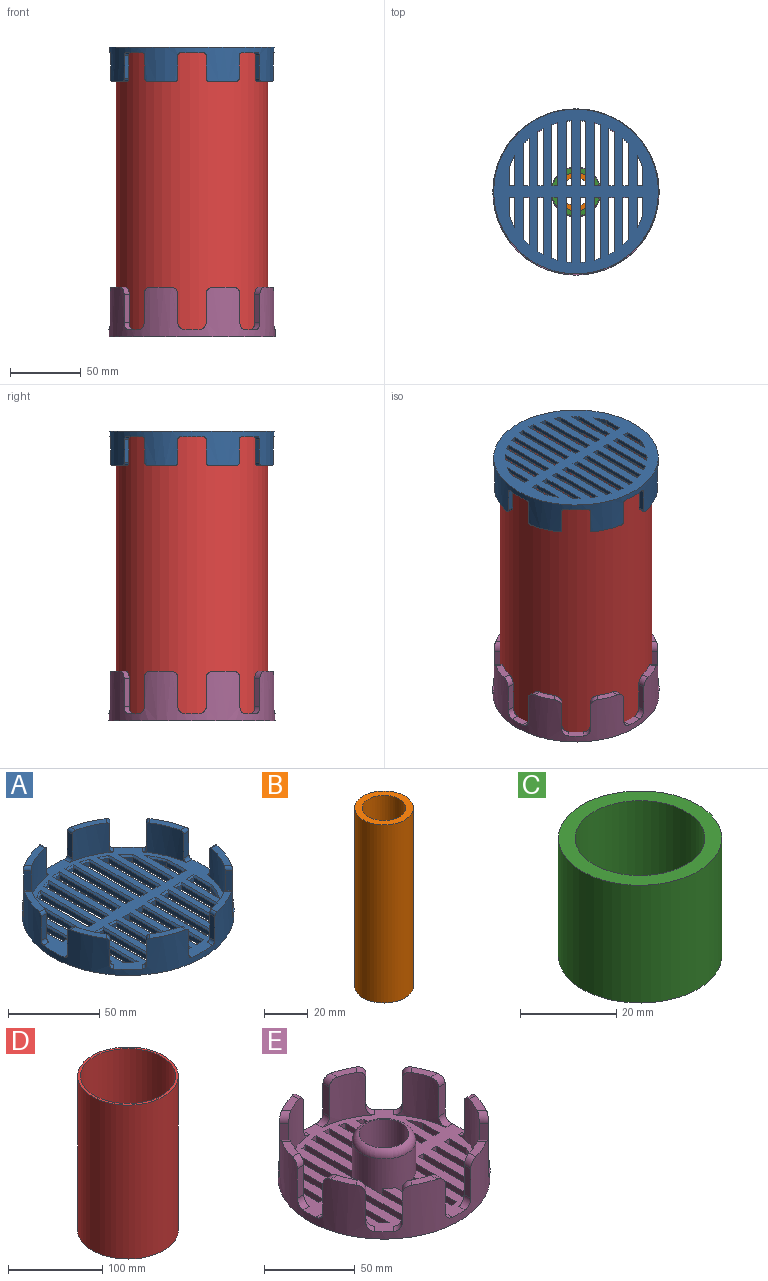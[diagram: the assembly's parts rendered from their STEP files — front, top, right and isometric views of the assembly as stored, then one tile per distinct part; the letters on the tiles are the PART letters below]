
ASSEMBLY  parts=5 mates=4
PART A: 223 faces, bbox 116x116x24 mm
  f0: plane 116x116mm, normal (0,0,-1), area 7720.4mm2, adj f2,f67,f68,f69,f70,f71,f72,f73
  f1: plane 116x116mm, normal (0,0,1), area 5149.1mm2, adj f2,f3,f4,f5,f6,f7,f8,f9
  f2: cylinder r=58mm len=116mm, axis (0,0,1), area 5530.1mm2, adj f0,f1,f10,f11,f12,f13,f14,f15
  f3: cylinder r=54mm len=24.11mm, axis (0,0,-1), area 445.9mm2, adj f1,f10,f19,f33,f42,f43,f51,f54
  f4: cylinder r=54mm len=24.11mm, axis (0,0,-1), area 445.9mm2, adj f1,f11,f32,f34,f41,f44,f53,f56
  f5: cylinder r=54mm len=24.11mm, axis (0,0,-1), area 445.9mm2, adj f1,f12,f30,f31,f40,f45,f55,f57
  f6: cylinder r=54mm len=24.11mm, axis (0,0,-1), area 445.9mm2, adj f1,f13,f26,f27,f37,f46,f62,f65
  f7: cylinder r=54mm len=24.11mm, axis (0,0,-1), area 445.9mm2, adj f1,f14,f24,f25,f36,f47,f60,f63
  f8: cylinder r=54mm len=24.11mm, axis (0,0,-1), area 445.9mm2, adj f1,f15,f22,f23,f35,f48,f58,f61
  f9: cylinder r=54mm len=24.11mm, axis (0,0,-1), area 445.9mm2, adj f1,f16,f20,f21,f49,f50,f52,f59
  f10: plane 19.64x11.03mm, normal (0,0,1), area 79.2mm2, adj f2,f3,f51,f54
  f11: plane 19.64x11.03mm, normal (0,0,1), area 79.2mm2, adj f2,f4,f53,f56
  f12: plane 19.64x11.03mm, normal (0,0,1), area 79.2mm2, adj f2,f5,f55,f57
  f13: plane 19.64x11.03mm, normal (0,0,1), area 79.2mm2, adj f2,f6,f62,f65
  f14: plane 19.64x11.03mm, normal (0,0,1), area 79.2mm2, adj f2,f7,f60,f63
  f15: plane 19.64x11.03mm, normal (0,0,1), area 79.2mm2, adj f2,f8,f58,f61
  f16: plane 19.64x11.03mm, normal (0,0,1), area 79.2mm2, adj f2,f9,f52,f59
  f17: cylinder r=54mm len=24.11mm, axis (0,0,-1), area 445.9mm2, adj f1,f18,f28,f29,f38,f39,f64,f66
  f18: plane 19.64x11.03mm, normal (0,0,1), area 79.2mm2, adj f2,f17,f64,f66
  f19: plane 16x4.07mm, normal (-1,0,0), area 65mm2, adj f2,f3,f42,f51
  f20: plane 16x4.07mm, normal (1,0,0), area 65mm2, adj f2,f9,f50,f52
  f21: plane 16x2.87mm, normal (-0.71,0.71,0), area 65mm2, adj f2,f9,f49,f59
  f22: plane 16x2.87mm, normal (0.71,-0.71,0), area 65mm2, adj f2,f8,f35,f58
  f23: plane 16x4.07mm, normal (0,1,0), area 65mm2, adj f2,f8,f48,f61
  f24: plane 16x4.07mm, normal (0,-1,0), area 65mm2, adj f2,f7,f36,f60
  f25: plane 16x2.87mm, normal (0.71,0.71,0), area 65mm2, adj f2,f7,f47,f63
  f26: plane 16x2.87mm, normal (-0.71,-0.71,0), area 65mm2, adj f2,f6,f37,f62
  f27: plane 16x4.07mm, normal (1,0,0), area 65mm2, adj f2,f6,f46,f65
  f28: plane 16x4.07mm, normal (-1,0,0), area 65mm2, adj f2,f17,f38,f64
  f29: plane 16x2.87mm, normal (0.71,-0.71,0), area 65mm2, adj f2,f17,f39,f66
  f30: plane 16x2.87mm, normal (-0.71,0.71,0), area 65mm2, adj f2,f5,f45,f57
  f31: plane 16x4.07mm, normal (0,-1,0), area 65mm2, adj f2,f5,f40,f55
  f32: plane 16x4.07mm, normal (0,1,0), area 65mm2, adj f2,f4,f44,f56
  f33: plane 16x2.87mm, normal (0.71,0.71,0), area 65mm2, adj f2,f3,f43,f54
  f34: plane 16x2.87mm, normal (-0.71,-0.71,0), area 65mm2, adj f2,f4,f41,f53
  f35: cylinder r=2mm len=4.51mm, axis (0.71,0.71,0), area 12.7mm2, adj f1,f2,f8,f22
  f36: cylinder r=2mm len=4.38mm, axis (1,0,0), area 12.7mm2, adj f1,f2,f7,f24
  f37: cylinder r=2mm len=4.51mm, axis (0.71,-0.71,0), area 12.7mm2, adj f1,f2,f6,f26
  f38: cylinder r=2mm len=4.38mm, axis (0,-1,0), area 12.7mm2, adj f1,f2,f17,f28
  f39: cylinder r=2mm len=4.51mm, axis (0.71,0.71,0), area 12.7mm2, adj f1,f2,f17,f29
  f40: cylinder r=2mm len=4.38mm, axis (1,0,0), area 12.7mm2, adj f1,f2,f5,f31
  f41: cylinder r=2mm len=4.51mm, axis (0.71,-0.71,0), area 12.7mm2, adj f1,f2,f4,f34
  f42: cylinder r=2mm len=4.38mm, axis (0,-1,0), area 12.7mm2, adj f1,f2,f3,f19
  f43: cylinder r=2mm len=4.51mm, axis (-0.71,0.71,0), area 12.7mm2, adj f1,f2,f3,f33
  f44: cylinder r=2mm len=4.38mm, axis (-1,0,0), area 12.7mm2, adj f1,f2,f4,f32
  f45: cylinder r=2mm len=4.51mm, axis (-0.71,-0.71,0), area 12.7mm2, adj f1,f2,f5,f30
  f46: cylinder r=2mm len=4.38mm, axis (0,1,0), area 12.7mm2, adj f1,f2,f6,f27
  f47: cylinder r=2mm len=4.51mm, axis (-0.71,0.71,0), area 12.7mm2, adj f1,f2,f7,f25
  f48: cylinder r=2mm len=4.38mm, axis (-1,0,0), area 12.7mm2, adj f1,f2,f8,f23
  f49: cylinder r=2mm len=4.51mm, axis (-0.71,-0.71,0), area 12.7mm2, adj f1,f2,f9,f21
  f50: cylinder r=2mm len=4.38mm, axis (0,1,0), area 12.7mm2, adj f1,f2,f9,f20
  f51: cylinder r=2mm len=4.48mm, axis (0,-1,0), area 12.8mm2, adj f2,f3,f10,f19
  f52: cylinder r=2mm len=4.48mm, axis (0,1,0), area 12.8mm2, adj f2,f9,f16,f20
  f53: cylinder r=2mm len=4.58mm, axis (0.71,-0.71,0), area 12.8mm2, adj f2,f4,f11,f34
  f54: cylinder r=2mm len=4.58mm, axis (-0.71,0.71,0), area 12.8mm2, adj f2,f3,f10,f33
  f55: cylinder r=2mm len=4.48mm, axis (1,0,0), area 12.8mm2, adj f2,f5,f12,f31
  f56: cylinder r=2mm len=4.48mm, axis (-1,0,0), area 12.8mm2, adj f2,f4,f11,f32
  f57: cylinder r=2mm len=4.58mm, axis (-0.71,-0.71,0), area 12.8mm2, adj f2,f5,f12,f30
  f58: cylinder r=2mm len=4.58mm, axis (0.71,0.71,0), area 12.8mm2, adj f2,f8,f15,f22
  f59: cylinder r=2mm len=4.58mm, axis (-0.71,-0.71,0), area 12.8mm2, adj f2,f9,f16,f21
  f60: cylinder r=2mm len=4.48mm, axis (1,0,0), area 12.8mm2, adj f2,f7,f14,f24
  f61: cylinder r=2mm len=4.48mm, axis (-1,0,0), area 12.8mm2, adj f2,f8,f15,f23
  f62: cylinder r=2mm len=4.58mm, axis (0.71,-0.71,0), area 12.8mm2, adj f2,f6,f13,f26
  f63: cylinder r=2mm len=4.58mm, axis (-0.71,0.71,0), area 12.8mm2, adj f2,f7,f14,f25
  f64: cylinder r=2mm len=4.48mm, axis (0,-1,0), area 12.8mm2, adj f2,f17,f18,f28
  f65: cylinder r=2mm len=4.48mm, axis (0,1,0), area 12.8mm2, adj f2,f6,f13,f27
  f66: cylinder r=2mm len=4.58mm, axis (0.71,0.71,0), area 12.8mm2, adj f2,f17,f18,f29
  f67: plane 43.02x3mm, normal (-1,0,0), area 129.1mm2, adj f0,f68,f70,f160
  f68: cylinder r=50mm len=4mm, axis (0,0,1), area 12.6mm2, adj f0,f67,f69,f159
  f69: plane 44.28x3mm, normal (1,0,0), area 132.8mm2, adj f0,f68,f70,f161
  f70: plane 4x3mm, normal (0,1,0), area 12mm2, adj f0,f67,f69,f162
  f71: plane 13.06x3mm, normal (1,0,0), area 39.2mm2, adj f0,f72,f74,f186
  f72: cylinder r=50mm len=8.46mm, axis (0,0,1), area 28.1mm2, adj f0,f71,f73,f188
  f73: plane 21.51x3mm, normal (-1,0,0), area 64.5mm2, adj f0,f72,f74,f187
  f74: plane 4x3mm, normal (0,-1,0), area 12mm2, adj f0,f71,f73,f185
  f75: plane 29.63x3mm, normal (1,0,0), area 88.9mm2, adj f0,f76,f78,f191
  f76: cylinder r=50mm len=4mm, axis (0,0,1), area 16.8mm2, adj f0,f75,f77,f189
  f77: plane 33.56x3mm, normal (-1,0,0), area 100.7mm2, adj f0,f76,f78,f190
  f78: plane 4x3mm, normal (0,-1,0), area 12mm2, adj f0,f75,f77,f192
  f79: plane 43.02x3mm, normal (1,0,0), area 129.1mm2, adj f0,f80,f82,f199
  f80: cylinder r=50mm len=4mm, axis (0,0,1), area 12.6mm2, adj f0,f79,f81,f197
  f81: plane 44.28x3mm, normal (-1,0,0), area 132.8mm2, adj f0,f80,f82,f198
  f82: plane 4x3mm, normal (0,-1,0), area 12mm2, adj f0,f79,f81,f200
  f83: plane 21.51x3mm, normal (-1,0,0), area 64.5mm2, adj f0,f84,f86,f184
  f84: cylinder r=50mm len=8.46mm, axis (0,0,1), area 28.1mm2, adj f0,f83,f85,f182
  f85: plane 13.06x3mm, normal (1,0,0), area 39.2mm2, adj f0,f84,f86,f181
  f86: plane 4x3mm, normal (0,1,0), area 12mm2, adj f0,f83,f85,f183
  f87: plane 33.56x3mm, normal (-1,0,0), area 100.7mm2, adj f0,f88,f90,f178
  f88: cylinder r=50mm len=4mm, axis (0,0,1), area 16.8mm2, adj f0,f87,f89,f180
  f89: plane 29.63x3mm, normal (1,0,0), area 88.9mm2, adj f0,f88,f90,f179
  f90: plane 4x3mm, normal (0,1,0), area 12mm2, adj f0,f87,f89,f177
  f91: plane 40.4x3mm, normal (-1,0,0), area 121.2mm2, adj f0,f92,f94,f174
  f92: cylinder r=50mm len=4mm, axis (0,0,1), area 13.9mm2, adj f0,f91,f93,f176
  f93: plane 38.08x3mm, normal (1,0,0), area 114.2mm2, adj f0,f92,f94,f175
  f94: plane 4x3mm, normal (0,1,0), area 12mm2, adj f0,f91,f93,f173
  f95: plane 44.28x3mm, normal (-1,0,0), area 132.8mm2, adj f0,f96,f98,f170
  f96: cylinder r=50mm len=4mm, axis (0,0,1), area 12.6mm2, adj f0,f95,f97,f172
  f97: plane 43.02x3mm, normal (1,0,0), area 129.1mm2, adj f0,f96,f98,f171
  f98: plane 4x3mm, normal (0,1,0), area 12mm2, adj f0,f95,f97,f169
  f99: plane 45.91x3mm, normal (-1,0,0), area 137.7mm2, adj f0,f100,f102,f168
  f100: cylinder r=50mm len=4mm, axis (0,0,1), area 12.1mm2, adj f0,f99,f101,f167
  f101: plane 45.51x3mm, normal (1,0,0), area 136.5mm2, adj f0,f100,f102,f166
  f102: plane 6x4mm, normal (0,1,0), area 17mm2, adj f0,f1,f99,f101,f166,f168
  f103: plane 45.51x3mm, normal (-1,0,0), area 136.5mm2, adj f0,f104,f106,f163
  f104: cylinder r=50mm len=4mm, axis (0,0,1), area 12.1mm2, adj f0,f103,f105,f165
  f105: plane 45.91x3mm, normal (1,0,0), area 137.7mm2, adj f0,f104,f106,f164
  f106: plane 6x4mm, normal (0,1,0), area 17mm2, adj f0,f1,f103,f105,f163,f164
  f107: plane 38.08x3mm, normal (-1,0,0), area 114.2mm2, adj f0,f108,f110,f156
  f108: cylinder r=50mm len=4mm, axis (0,0,1), area 13.9mm2, adj f0,f107,f109,f155
  f109: plane 40.4x3mm, normal (1,0,0), area 121.2mm2, adj f0,f108,f110,f157
  f110: plane 4x3mm, normal (0,1,0), area 12mm2, adj f0,f107,f109,f158
  f111: plane 13.06x3mm, normal (-1,0,0), area 39.2mm2, adj f0,f112,f114,f152
  f112: cylinder r=50mm len=8.46mm, axis (0,0,1), area 28.1mm2, adj f0,f111,f113,f154
  f113: plane 21.51x3mm, normal (1,0,0), area 64.5mm2, adj f0,f112,f114,f153
  f114: plane 4x3mm, normal (0,1,0), area 12mm2, adj f0,f111,f113,f151
  f115: plane 38.08x3mm, normal (1,0,0), area 114.2mm2, adj f0,f116,f118,f195
  f116: cylinder r=50mm len=4mm, axis (0,0,1), area 13.9mm2, adj f0,f115,f117,f193
  f117: plane 40.4x3mm, normal (-1,0,0), area 121.2mm2, adj f0,f116,f118,f194
  f118: plane 4x3mm, normal (0,-1,0), area 12mm2, adj f0,f115,f117,f196
  f119: plane 43.02x3mm, normal (-1,0,0), area 129.1mm2, adj f0,f120,f122,f208
  f120: plane 4x3mm, normal (0,-1,0), area 12mm2, adj f0,f119,f121,f210
  f121: plane 44.28x3mm, normal (1,0,0), area 132.8mm2, adj f0,f120,f122,f209
  f122: cylinder r=50mm len=4mm, axis (0,0,1), area 12.6mm2, adj f0,f119,f121,f207
  f123: plane 38.08x3mm, normal (-1,0,0), area 114.2mm2, adj f0,f124,f126,f212
  f124: plane 4x3mm, normal (0,-1,0), area 12mm2, adj f0,f123,f125,f214
  f125: plane 40.4x3mm, normal (1,0,0), area 121.2mm2, adj f0,f124,f126,f213
  f126: cylinder r=50mm len=4mm, axis (0,0,1), area 13.9mm2, adj f0,f123,f125,f211
  f127: plane 4x3mm, normal (0,-1,0), area 12mm2, adj f0,f128,f130,f222
  f128: plane 21.51x3mm, normal (1,0,0), area 64.5mm2, adj f0,f127,f129,f221
  f129: cylinder r=50mm len=8.46mm, axis (0,0,1), area 28.1mm2, adj f0,f128,f130,f219
  f130: plane 13.06x3mm, normal (-1,0,0), area 39.2mm2, adj f0,f127,f129,f220
  f131: plane 29.63x3mm, normal (-1,0,0), area 88.9mm2, adj f0,f132,f134,f148
  f132: cylinder r=50mm len=4mm, axis (0,0,1), area 16.8mm2, adj f0,f131,f133,f150
  f133: plane 33.56x3mm, normal (1,0,0), area 100.7mm2, adj f0,f132,f134,f149
  f134: plane 4x3mm, normal (0,1,0), area 12mm2, adj f0,f131,f133,f147
  f135: plane 45.51x3mm, normal (1,0,0), area 136.5mm2, adj f0,f136,f138,f203
  f136: cylinder r=50mm len=4mm, axis (0,0,1), area 12.1mm2, adj f0,f135,f137,f202
  f137: plane 45.91x3mm, normal (-1,0,0), area 137.7mm2, adj f0,f136,f138,f201
  f138: plane 6x4mm, normal (0,-1,0), area 17mm2, adj f0,f1,f135,f137,f201,f203
  f139: plane 45.91x3mm, normal (1,0,0), area 137.7mm2, adj f0,f140,f142,f204
  f140: cylinder r=50mm len=4mm, axis (0,0,1), area 12.1mm2, adj f0,f139,f141,f205
  f141: plane 45.51x3mm, normal (-1,0,0), area 136.5mm2, adj f0,f140,f142,f206
  f142: plane 6x4mm, normal (0,-1,0), area 17mm2, adj f0,f1,f139,f141,f204,f206
  f143: plane 29.63x3mm, normal (-1,0,0), area 88.9mm2, adj f0,f144,f146,f216
  f144: plane 4x3mm, normal (0,-1,0), area 12mm2, adj f0,f143,f145,f218
  f145: plane 33.56x3mm, normal (1,0,0), area 100.7mm2, adj f0,f144,f146,f217
  f146: cylinder r=50mm len=4mm, axis (0,0,1), area 16.8mm2, adj f0,f143,f145,f215
  f147: plane 6x1mm, normal (0,0.71,0.71), area 7.1mm2, adj f1,f134,f148,f149
  f148: plane 31.02x1mm, normal (-0.71,0,0.71), area 42.9mm2, adj f1,f131,f147,f150
  f149: plane 36.74x1.02mm, normal (0.71,0,0.71), area 49.7mm2, adj f1,f133,f147,f150
  f150: cone r=50mm half-angle=45deg, axis (0,0,1), area 9.8mm2, adj f1,f132,f148,f149
  f151: plane 6x1mm, normal (0,0.71,0.71), area 7.1mm2, adj f1,f114,f152,f153
  f152: plane 14.23x1mm, normal (-0.71,0,0.71), area 19.3mm2, adj f1,f111,f151,f154
  f153: plane 25.93x1mm, normal (0.71,0,0.71), area 33.6mm2, adj f1,f113,f151,f154
  f154: cone r=50mm half-angle=45deg, axis (0,0,1), area 16mm2, adj f1,f112,f152,f153
  f155: cone r=50mm half-angle=45deg, axis (0,0,1), area 8.1mm2, adj f1,f108,f156,f157
  f156: plane 39.63x1mm, normal (-0.71,0,0.71), area 54.9mm2, adj f1,f107,f155,f158
  f157: plane 43.03x1.02mm, normal (0.71,0,0.71), area 59mm2, adj f1,f109,f155,f158
  f158: plane 6x1mm, normal (0,0.71,0.71), area 7.1mm2, adj f1,f110,f156,f157
  f159: cone r=50mm half-angle=45deg, axis (0,0,1), area 7.4mm2, adj f1,f68,f160,f161
  f160: plane 44.72x1.01mm, normal (-0.71,0,0.71), area 62mm2, adj f1,f67,f159,f162
  f161: plane 46.58x1.01mm, normal (0.71,0,0.71), area 64.2mm2, adj f1,f69,f159,f162
  f162: plane 6x1mm, normal (0,0.71,0.71), area 7.1mm2, adj f1,f70,f160,f161
  f163: plane 46.38x1.01mm, normal (-0.71,0,0.71), area 65mm2, adj f1,f103,f106,f165
  f164: plane 46.97x1.01mm, normal (0.71,0,0.71), area 65.7mm2, adj f1,f105,f106,f165
  f165: cone r=50mm half-angle=45deg, axis (0,0,1), area 7.1mm2, adj f1,f104,f163,f164
  f166: plane 46.38x1.01mm, normal (0.71,0,0.71), area 65mm2, adj f1,f101,f102,f167
  f167: cone r=50mm half-angle=45deg, axis (0,0,1), area 7.1mm2, adj f1,f100,f166,f168
  f168: plane 46.97x1.01mm, normal (-0.71,0,0.71), area 65.7mm2, adj f1,f99,f102,f167
  f169: plane 6x1mm, normal (0,0.71,0.71), area 7.1mm2, adj f1,f98,f170,f171
  f170: plane 46.58x1.01mm, normal (-0.71,0,0.71), area 64.2mm2, adj f1,f95,f169,f172
  f171: plane 44.72x1.01mm, normal (0.71,0,0.71), area 62mm2, adj f1,f97,f169,f172
  f172: cone r=50mm half-angle=45deg, axis (0,0,1), area 7.4mm2, adj f1,f96,f170,f171
  f173: plane 6x1mm, normal (0,0.71,0.71), area 7.1mm2, adj f1,f94,f174,f175
  f174: plane 43.03x1.02mm, normal (-0.71,0,0.71), area 59mm2, adj f1,f91,f173,f176
  f175: plane 39.63x1mm, normal (0.71,0,0.71), area 54.9mm2, adj f1,f93,f173,f176
  f176: cone r=50mm half-angle=45deg, axis (0,0,1), area 8.1mm2, adj f1,f92,f174,f175
  f177: plane 6x1mm, normal (0,0.71,0.71), area 7.1mm2, adj f1,f90,f178,f179
  f178: plane 36.74x1.02mm, normal (-0.71,0,0.71), area 49.7mm2, adj f1,f87,f177,f180
  f179: plane 31.02x1mm, normal (0.71,0,0.71), area 42.9mm2, adj f1,f89,f177,f180
  f180: cone r=50mm half-angle=45deg, axis (0,0,1), area 9.8mm2, adj f1,f88,f178,f179
  f181: plane 14.23x1mm, normal (0.71,0,0.71), area 19.3mm2, adj f1,f85,f182,f183
  f182: cone r=50mm half-angle=45deg, axis (0,0,1), area 16mm2, adj f1,f84,f181,f184
  f183: plane 6x1mm, normal (0,0.71,0.71), area 7.1mm2, adj f1,f86,f181,f184
  f184: plane 25.93x1mm, normal (-0.71,0,0.71), area 33.6mm2, adj f1,f83,f182,f183
  f185: plane 6x1mm, normal (0,-0.71,0.71), area 7.1mm2, adj f1,f74,f186,f187
  f186: plane 14.23x1mm, normal (0.71,0,0.71), area 19.3mm2, adj f1,f71,f185,f188
  f187: plane 25.93x1mm, normal (-0.71,0,0.71), area 33.6mm2, adj f1,f73,f185,f188
  f188: cone r=50mm half-angle=45deg, axis (0,0,1), area 16mm2, adj f1,f72,f186,f187
  f189: cone r=50mm half-angle=45deg, axis (0,0,1), area 9.8mm2, adj f1,f76,f190,f191
  f190: plane 36.74x1.02mm, normal (-0.71,0,0.71), area 49.7mm2, adj f1,f77,f189,f192
  f191: plane 31.02x1mm, normal (0.71,0,0.71), area 42.9mm2, adj f1,f75,f189,f192
  f192: plane 6x1mm, normal (0,-0.71,0.71), area 7.1mm2, adj f1,f78,f190,f191
  f193: cone r=50mm half-angle=45deg, axis (0,0,1), area 8.1mm2, adj f1,f116,f194,f195
  f194: plane 43.03x1.02mm, normal (-0.71,0,0.71), area 59mm2, adj f1,f117,f193,f196
  f195: plane 39.63x1mm, normal (0.71,0,0.71), area 54.9mm2, adj f1,f115,f193,f196
  f196: plane 6x1mm, normal (0,-0.71,0.71), area 7.1mm2, adj f1,f118,f194,f195
  f197: cone r=50mm half-angle=45deg, axis (0,0,1), area 7.4mm2, adj f1,f80,f198,f199
  f198: plane 46.58x1.01mm, normal (-0.71,0,0.71), area 64.2mm2, adj f1,f81,f197,f200
  f199: plane 44.72x1.01mm, normal (0.71,0,0.71), area 62mm2, adj f1,f79,f197,f200
  f200: plane 6x1mm, normal (0,-0.71,0.71), area 7.1mm2, adj f1,f82,f198,f199
  f201: plane 46.97x1.01mm, normal (-0.71,0,0.71), area 65.7mm2, adj f1,f137,f138,f202
  f202: cone r=50mm half-angle=45deg, axis (0,0,1), area 7.1mm2, adj f1,f136,f201,f203
  f203: plane 46.38x1.01mm, normal (0.71,0,0.71), area 65mm2, adj f1,f135,f138,f202
  f204: plane 46.97x1.01mm, normal (0.71,0,0.71), area 65.7mm2, adj f1,f139,f142,f205
  f205: cone r=50mm half-angle=45deg, axis (0,0,1), area 7.1mm2, adj f1,f140,f204,f206
  f206: plane 46.38x1.01mm, normal (-0.71,0,0.71), area 65mm2, adj f1,f141,f142,f205
  f207: cone r=50mm half-angle=45deg, axis (0,0,1), area 7.4mm2, adj f1,f122,f208,f209
  f208: plane 44.72x1.01mm, normal (-0.71,0,0.71), area 62mm2, adj f1,f119,f207,f210
  f209: plane 46.58x1.01mm, normal (0.71,0,0.71), area 64.2mm2, adj f1,f121,f207,f210
  f210: plane 6x1mm, normal (0,-0.71,0.71), area 7.1mm2, adj f1,f120,f208,f209
  f211: cone r=50mm half-angle=45deg, axis (0,0,1), area 8.1mm2, adj f1,f126,f212,f213
  f212: plane 39.63x1mm, normal (-0.71,0,0.71), area 54.9mm2, adj f1,f123,f211,f214
  f213: plane 43.03x1.02mm, normal (0.71,0,0.71), area 59mm2, adj f1,f125,f211,f214
  f214: plane 6x1mm, normal (0,-0.71,0.71), area 7.1mm2, adj f1,f124,f212,f213
  f215: cone r=50mm half-angle=45deg, axis (0,0,1), area 9.8mm2, adj f1,f146,f216,f217
  f216: plane 31.02x1mm, normal (-0.71,0,0.71), area 42.9mm2, adj f1,f143,f215,f218
  f217: plane 36.74x1.02mm, normal (0.71,0,0.71), area 49.7mm2, adj f1,f145,f215,f218
  f218: plane 6x1mm, normal (0,-0.71,0.71), area 7.1mm2, adj f1,f144,f216,f217
  f219: cone r=50mm half-angle=45deg, axis (0,0,1), area 16mm2, adj f1,f129,f220,f221
  f220: plane 14.23x1mm, normal (-0.71,0,0.71), area 19.3mm2, adj f1,f130,f219,f222
  f221: plane 25.93x1mm, normal (0.71,0,0.71), area 33.6mm2, adj f1,f128,f219,f222
  f222: plane 6x1mm, normal (0,-0.71,0.71), area 7.1mm2, adj f1,f127,f220,f221
PART B: 4 faces, bbox 27x27x100 mm
  f0: cylinder r=10mm len=100mm, axis (0,0,-1), area 6283.2mm2, adj f2,f3
  f1: cylinder r=13.5mm len=100mm, axis (0,0,-1), area 8482.3mm2, adj f2,f3
  f2: plane 27x27mm, normal (0,0,1), area 258.4mm2, adj f0,f1
  f3: plane 27x27mm, normal (0,0,-1), area 258.4mm2, adj f0,f1
PART C: 4 faces, bbox 34x34x30 mm
  f0: cylinder r=13.5mm len=30mm, axis (0,0,-1), area 2544.7mm2, adj f2,f3
  f1: cylinder r=17mm len=34mm, axis (0,0,-1), area 3204.4mm2, adj f2,f3
  f2: plane 34x34mm, normal (0,0,1), area 335.4mm2, adj f0,f1
  f3: plane 34x34mm, normal (0,0,-1), area 335.4mm2, adj f0,f1
PART D: 4 faces, bbox 107x107x200 mm
  f0: cylinder r=50.5mm len=200mm, axis (0,0,-1), area 63460.2mm2, adj f2,f3
  f1: cylinder r=53.5mm len=200mm, axis (0,0,-1), area 67230.1mm2, adj f2,f3
  f2: plane 107x107mm, normal (0,0,1), area 980.2mm2, adj f0,f1
  f3: plane 107x107mm, normal (0,0,-1), area 980.2mm2, adj f0,f1
PART E: 142 faces, bbox 117x117x35 mm
  f0: plane 117x117mm, normal (0,0,1), area 5861.2mm2, adj f2,f3,f4,f5,f6,f7,f8,f9
  f1: plane 117x117mm, normal (0,0,-1), area 7588.1mm2, adj f2,f17,f36,f70,f71,f72,f73,f74
  f2: cylinder r=58.5mm len=117mm, axis (0,0,1), area 8040.6mm2, adj f0,f1,f10,f11,f12,f13,f14,f15
  f3: cylinder r=53.5mm len=30mm, axis (0,0,-1), area 656.9mm2, adj f0,f10,f20,f34,f45,f46,f54,f57
  f4: cylinder r=53.5mm len=30mm, axis (0,0,-1), area 656.9mm2, adj f0,f11,f33,f35,f44,f47,f56,f59
  f5: cylinder r=53.5mm len=30mm, axis (0,0,-1), area 656.9mm2, adj f0,f12,f31,f32,f43,f48,f58,f60
  f6: cylinder r=53.5mm len=30mm, axis (0,0,-1), area 656.9mm2, adj f0,f13,f27,f28,f40,f49,f65,f68
  f7: cylinder r=53.5mm len=30mm, axis (0,0,-1), area 656.9mm2, adj f0,f14,f25,f26,f39,f50,f63,f66
  f8: cylinder r=53.5mm len=30mm, axis (0,0,-1), area 656.9mm2, adj f0,f15,f23,f24,f38,f51,f61,f64
  f9: cylinder r=53.5mm len=30mm, axis (0,0,-1), area 656.9mm2, adj f0,f16,f21,f22,f52,f53,f55,f62
  f10: plane 14.38x9.62mm, normal (0,0,1), area 68.1mm2, adj f2,f3,f54,f57
  f11: plane 14.38x9.62mm, normal (0,0,1), area 68.1mm2, adj f2,f4,f56,f59
  f12: plane 14.38x9.62mm, normal (0,0,1), area 68.1mm2, adj f2,f5,f58,f60
  f13: plane 14.38x9.62mm, normal (0,0,1), area 68.1mm2, adj f2,f6,f65,f68
  f14: plane 14.38x9.62mm, normal (0,0,1), area 68.1mm2, adj f2,f7,f63,f66
  f15: plane 14.38x9.62mm, normal (0,0,1), area 68.1mm2, adj f2,f8,f61,f64
  f16: plane 14.38x9.62mm, normal (0,0,1), area 68.1mm2, adj f2,f9,f55,f62
  f17: cylinder r=13.75mm len=30mm, axis (0,0,1), area 2591.8mm2, adj f1,f37
  f18: cylinder r=53.5mm len=30mm, axis (0,0,-1), area 656.9mm2, adj f0,f19,f29,f30,f41,f42,f67,f69
  f19: plane 14.38x9.62mm, normal (0,0,1), area 68.1mm2, adj f2,f18,f67,f69
  f20: plane 20x5.08mm, normal (-1,0,0), area 101.6mm2, adj f2,f3,f45,f54
  f21: plane 20x5.08mm, normal (1,0,0), area 101.6mm2, adj f2,f9,f53,f55
  f22: plane 20x3.59mm, normal (-0.71,0.71,0), area 101.6mm2, adj f2,f9,f52,f62
  f23: plane 20x3.59mm, normal (0.71,-0.71,0), area 101.6mm2, adj f2,f8,f38,f61
  f24: plane 20x5.08mm, normal (0,1,0), area 101.6mm2, adj f2,f8,f51,f64
  f25: plane 20x5.08mm, normal (0,-1,0), area 101.6mm2, adj f2,f7,f39,f63
  f26: plane 20x3.59mm, normal (0.71,0.71,0), area 101.6mm2, adj f2,f7,f50,f66
  f27: plane 20x3.59mm, normal (-0.71,-0.71,0), area 101.6mm2, adj f2,f6,f40,f65
  f28: plane 20x5.08mm, normal (1,0,0), area 101.6mm2, adj f2,f6,f49,f68
  f29: plane 20x5.08mm, normal (-1,0,0), area 101.6mm2, adj f2,f18,f41,f67
  f30: plane 20x3.59mm, normal (0.71,-0.71,0), area 101.6mm2, adj f2,f18,f42,f69
  f31: plane 20x3.59mm, normal (-0.71,0.71,0), area 101.6mm2, adj f2,f5,f48,f60
  f32: plane 20x5.08mm, normal (0,-1,0), area 101.6mm2, adj f2,f5,f43,f58
  f33: plane 20x5.08mm, normal (0,1,0), area 101.6mm2, adj f2,f4,f47,f59
  f34: plane 20x3.59mm, normal (0.71,0.71,0), area 101.6mm2, adj f2,f3,f46,f57
  f35: plane 20x3.59mm, normal (-0.71,-0.71,0), area 101.6mm2, adj f2,f4,f44,f56
  f36: cylinder r=17.5mm len=35mm, axis (0,0,-1), area 2473.2mm2, adj f0,f1,f37,f71,f72,f81,f82,f97
  f37: torus R=12.5mm, axis (0,0,1), area 669.7mm2, adj f17,f36
  f38: cylinder r=5mm len=7.59mm, axis (0.71,0.71,0), area 39.7mm2, adj f0,f2,f8,f23
  f39: cylinder r=5mm len=5.73mm, axis (1,0,0), area 39.7mm2, adj f0,f2,f7,f25
  f40: cylinder r=5mm len=7.59mm, axis (0.71,-0.71,0), area 39.7mm2, adj f0,f2,f6,f27
  f41: cylinder r=5mm len=5.73mm, axis (0,-1,0), area 39.7mm2, adj f0,f2,f18,f29
  f42: cylinder r=5mm len=7.59mm, axis (0.71,0.71,0), area 39.7mm2, adj f0,f2,f18,f30
  f43: cylinder r=5mm len=5.73mm, axis (1,0,0), area 39.7mm2, adj f0,f2,f5,f32
  f44: cylinder r=5mm len=7.59mm, axis (0.71,-0.71,0), area 39.7mm2, adj f0,f2,f4,f35
  f45: cylinder r=5mm len=5.73mm, axis (0,-1,0), area 39.7mm2, adj f0,f2,f3,f20
  f46: cylinder r=5mm len=7.59mm, axis (-0.71,0.71,0), area 39.7mm2, adj f0,f2,f3,f34
  f47: cylinder r=5mm len=5.73mm, axis (-1,0,0), area 39.7mm2, adj f0,f2,f4,f33
  f48: cylinder r=5mm len=7.59mm, axis (-0.71,-0.71,0), area 39.7mm2, adj f0,f2,f5,f31
  f49: cylinder r=5mm len=5.73mm, axis (0,1,0), area 39.7mm2, adj f0,f2,f6,f28
  f50: cylinder r=5mm len=7.59mm, axis (-0.71,0.71,0), area 39.7mm2, adj f0,f2,f7,f26
  f51: cylinder r=5mm len=5.73mm, axis (-1,0,0), area 39.7mm2, adj f0,f2,f8,f24
  f52: cylinder r=5mm len=7.59mm, axis (-0.71,-0.71,0), area 39.7mm2, adj f0,f2,f9,f22
  f53: cylinder r=5mm len=5.73mm, axis (0,1,0), area 39.7mm2, adj f0,f2,f9,f21
  f54: cylinder r=5mm len=6.29mm, axis (0,-1,0), area 40.2mm2, adj f2,f3,f10,f20
  f55: cylinder r=5mm len=6.29mm, axis (0,1,0), area 40.2mm2, adj f2,f9,f16,f21
  f56: cylinder r=5mm len=7.98mm, axis (0.71,-0.71,0), area 40.2mm2, adj f2,f4,f11,f35
  f57: cylinder r=5mm len=7.98mm, axis (-0.71,0.71,0), area 40.2mm2, adj f2,f3,f10,f34
  f58: cylinder r=5mm len=6.29mm, axis (1,0,0), area 40.2mm2, adj f2,f5,f12,f32
  f59: cylinder r=5mm len=6.29mm, axis (-1,0,0), area 40.2mm2, adj f2,f4,f11,f33
  f60: cylinder r=5mm len=7.98mm, axis (-0.71,-0.71,0), area 40.2mm2, adj f2,f5,f12,f31
  f61: cylinder r=5mm len=7.98mm, axis (0.71,0.71,0), area 40.2mm2, adj f2,f8,f15,f23
  f62: cylinder r=5mm len=7.98mm, axis (-0.71,-0.71,0), area 40.2mm2, adj f2,f9,f16,f22
  f63: cylinder r=5mm len=6.29mm, axis (1,0,0), area 40.2mm2, adj f2,f7,f14,f25
  f64: cylinder r=5mm len=6.29mm, axis (-1,0,0), area 40.2mm2, adj f2,f8,f15,f24
  f65: cylinder r=5mm len=7.98mm, axis (0.71,-0.71,0), area 40.2mm2, adj f2,f6,f13,f27
  f66: cylinder r=5mm len=7.98mm, axis (-0.71,0.71,0), area 40.2mm2, adj f2,f7,f14,f26
  f67: cylinder r=5mm len=6.29mm, axis (0,-1,0), area 40.2mm2, adj f2,f18,f19,f29
  f68: cylinder r=5mm len=6.29mm, axis (0,1,0), area 40.2mm2, adj f2,f6,f13,f28
  f69: cylinder r=5mm len=7.98mm, axis (0.71,0.71,0), area 40.2mm2, adj f2,f18,f19,f30
  f70: cylinder r=50mm len=5mm, axis (0,0,1), area 21mm2, adj f0,f1,f71,f72
  f71: plane 36.57x5mm, normal (1,0,0), area 182.8mm2, adj f0,f1,f36,f70
  f72: plane 42.87x5mm, normal (-1,0,0), area 214.3mm2, adj f0,f1,f36,f70
  f73: plane 21.51x5mm, normal (-1,0,0), area 107.6mm2, adj f0,f1,f74,f76
  f74: plane 5x4mm, normal (0,-1,0), area 20mm2, adj f0,f1,f73,f75
  f75: plane 13.06x5mm, normal (1,0,0), area 65.3mm2, adj f0,f1,f74,f76
  f76: cylinder r=50mm len=8.46mm, axis (0,0,1), area 46.8mm2, adj f0,f1,f73,f75
  f77: plane 33.56x5mm, normal (-1,0,0), area 167.8mm2, adj f0,f1,f78,f80
  f78: plane 5x4mm, normal (0,-1,0), area 20mm2, adj f0,f1,f77,f79
  f79: plane 29.63x5mm, normal (1,0,0), area 148.2mm2, adj f0,f1,f78,f80
  f80: cylinder r=50mm len=5mm, axis (0,0,1), area 28.1mm2, adj f0,f1,f77,f79
  f81: plane 36.57x5mm, normal (-1,0,0), area 182.8mm2, adj f0,f1,f36,f83
  f82: plane 42.87x5mm, normal (1,0,0), area 214.3mm2, adj f0,f1,f36,f83
  f83: cylinder r=50mm len=5mm, axis (0,0,1), area 21mm2, adj f0,f1,f81,f82
  f84: plane 21.51x5mm, normal (-1,0,0), area 107.6mm2, adj f0,f1,f85,f87
  f85: cylinder r=50mm len=8.46mm, axis (0,0,1), area 46.8mm2, adj f0,f1,f84,f86
  f86: plane 13.06x5mm, normal (1,0,0), area 65.3mm2, adj f0,f1,f85,f87
  f87: plane 5x4mm, normal (0,1,0), area 20mm2, adj f0,f1,f84,f86
  f88: cylinder r=50mm len=5mm, axis (0,0,1), area 28.1mm2, adj f0,f1,f89,f91
  f89: plane 29.63x5mm, normal (1,0,0), area 148.2mm2, adj f0,f1,f88,f90
  f90: plane 5x4mm, normal (0,1,0), area 20mm2, adj f0,f1,f89,f91
  f91: plane 33.56x5mm, normal (-1,0,0), area 167.8mm2, adj f0,f1,f88,f90
  f92: cylinder r=50mm len=5mm, axis (0,0,1), area 23.1mm2, adj f0,f1,f93,f95
  f93: plane 38.08x5mm, normal (1,0,0), area 190.4mm2, adj f0,f1,f92,f94
  f94: plane 5x4mm, normal (0,1,0), area 20mm2, adj f0,f1,f93,f95
  f95: plane 40.4x5mm, normal (-1,0,0), area 202mm2, adj f0,f1,f92,f94
  f96: cylinder r=50mm len=5mm, axis (0,0,1), area 21mm2, adj f0,f1,f97,f98
  f97: plane 42.87x5mm, normal (1,0,0), area 214.3mm2, adj f0,f1,f36,f96
  f98: plane 36.57x5mm, normal (-1,0,0), area 182.8mm2, adj f0,f1,f36,f96
  f99: cylinder r=50mm len=5mm, axis (0,0,1), area 20.1mm2, adj f0,f1,f100,f101
  f100: plane 33.47x5mm, normal (1,0,0), area 167.3mm2, adj f0,f1,f36,f99
  f101: plane 32.67x5mm, normal (-1,0,0), area 163.3mm2, adj f0,f1,f36,f99
  f102: cylinder r=50mm len=5mm, axis (0,0,1), area 20.1mm2, adj f0,f1,f103,f104
  f103: plane 32.67x5mm, normal (1,0,0), area 163.3mm2, adj f0,f1,f36,f102
  f104: plane 33.47x5mm, normal (-1,0,0), area 167.3mm2, adj f0,f1,f36,f102
  f105: cylinder r=50mm len=5mm, axis (0,0,1), area 23.1mm2, adj f0,f1,f106,f108
  f106: plane 40.4x5mm, normal (1,0,0), area 202mm2, adj f0,f1,f105,f107
  f107: plane 5x4mm, normal (0,1,0), area 20mm2, adj f0,f1,f106,f108
  f108: plane 38.08x5mm, normal (-1,0,0), area 190.4mm2, adj f0,f1,f105,f107
  f109: cylinder r=50mm len=8.46mm, axis (0,0,1), area 46.8mm2, adj f0,f1,f110,f112
  f110: plane 21.51x5mm, normal (1,0,0), area 107.6mm2, adj f0,f1,f109,f111
  f111: plane 5x4mm, normal (0,1,0), area 20mm2, adj f0,f1,f110,f112
  f112: plane 13.06x5mm, normal (-1,0,0), area 65.3mm2, adj f0,f1,f109,f111
  f113: plane 40.4x5mm, normal (-1,0,0), area 202mm2, adj f0,f1,f114,f116
  f114: plane 5x4mm, normal (0,-1,0), area 20mm2, adj f0,f1,f113,f115
  f115: plane 38.08x5mm, normal (1,0,0), area 190.4mm2, adj f0,f1,f114,f116
  f116: cylinder r=50mm len=5mm, axis (0,0,1), area 23.1mm2, adj f0,f1,f113,f115
  f117: plane 36.57x5mm, normal (1,0,0), area 182.8mm2, adj f0,f1,f36,f118
  f118: cylinder r=50mm len=5mm, axis (0,0,1), area 21mm2, adj f0,f1,f117,f119
  f119: plane 42.87x5mm, normal (-1,0,0), area 214.3mm2, adj f0,f1,f36,f118
  f120: plane 38.08x5mm, normal (-1,0,0), area 190.4mm2, adj f0,f1,f121,f123
  f121: plane 5x4mm, normal (0,-1,0), area 20mm2, adj f0,f1,f120,f122
  f122: plane 40.4x5mm, normal (1,0,0), area 202mm2, adj f0,f1,f121,f123
  f123: cylinder r=50mm len=5mm, axis (0,0,1), area 23.1mm2, adj f0,f1,f120,f122
  f124: plane 13.06x5mm, normal (-1,0,0), area 65.3mm2, adj f0,f1,f125,f127
  f125: plane 5x4mm, normal (0,-1,0), area 20mm2, adj f0,f1,f124,f126
  f126: plane 21.51x5mm, normal (1,0,0), area 107.6mm2, adj f0,f1,f125,f127
  f127: cylinder r=50mm len=8.46mm, axis (0,0,1), area 46.8mm2, adj f0,f1,f124,f126
  f128: cylinder r=50mm len=5mm, axis (0,0,1), area 28.1mm2, adj f0,f1,f129,f131
  f129: plane 33.56x5mm, normal (1,0,0), area 167.8mm2, adj f0,f1,f128,f130
  f130: plane 5x4mm, normal (0,1,0), area 20mm2, adj f0,f1,f129,f131
  f131: plane 29.63x5mm, normal (-1,0,0), area 148.2mm2, adj f0,f1,f128,f130
  f132: plane 32.67x5mm, normal (-1,0,0), area 163.3mm2, adj f0,f1,f36,f134
  f133: plane 33.47x5mm, normal (1,0,0), area 167.3mm2, adj f0,f1,f36,f134
  f134: cylinder r=50mm len=5mm, axis (0,0,1), area 20.1mm2, adj f0,f1,f132,f133
  f135: plane 33.47x5mm, normal (-1,0,0), area 167.3mm2, adj f0,f1,f36,f137
  f136: plane 32.67x5mm, normal (1,0,0), area 163.3mm2, adj f0,f1,f36,f137
  f137: cylinder r=50mm len=5mm, axis (0,0,1), area 20.1mm2, adj f0,f1,f135,f136
  f138: plane 29.63x5mm, normal (-1,0,0), area 148.2mm2, adj f0,f1,f139,f141
  f139: plane 5x4mm, normal (0,-1,0), area 20mm2, adj f0,f1,f138,f140
  f140: plane 33.56x5mm, normal (1,0,0), area 167.8mm2, adj f0,f1,f139,f141
  f141: cylinder r=50mm len=5mm, axis (0,0,1), area 28.1mm2, adj f0,f1,f138,f140
PLACE A rot(axis=(0,-1,0),180deg) t=(8.04,55.53,231.53)mm
PLACE B t=(8.04,55.53,31.53)mm
PLACE C t=(8.04,55.53,131.53)mm
PLACE D t=(8.04,55.53,31.53)mm
PLACE E t=(8.04,55.53,36.53)mm
MATE fastened C.f1 <-> D.f1  axis (0,0,-1) through (8.04,55.53,131.53)mm
MATE fastened B.f1 <-> E.f17  axis (0,0,-1) through (8.04,55.53,31.53)mm
MATE fastened E.f17 <-> D.f0  axis (0,0,1) through (8.04,55.53,31.53)mm
MATE fastened A.f136 <-> D.f0  axis (0,0,-1) through (8.04,55.53,231.53)mm
